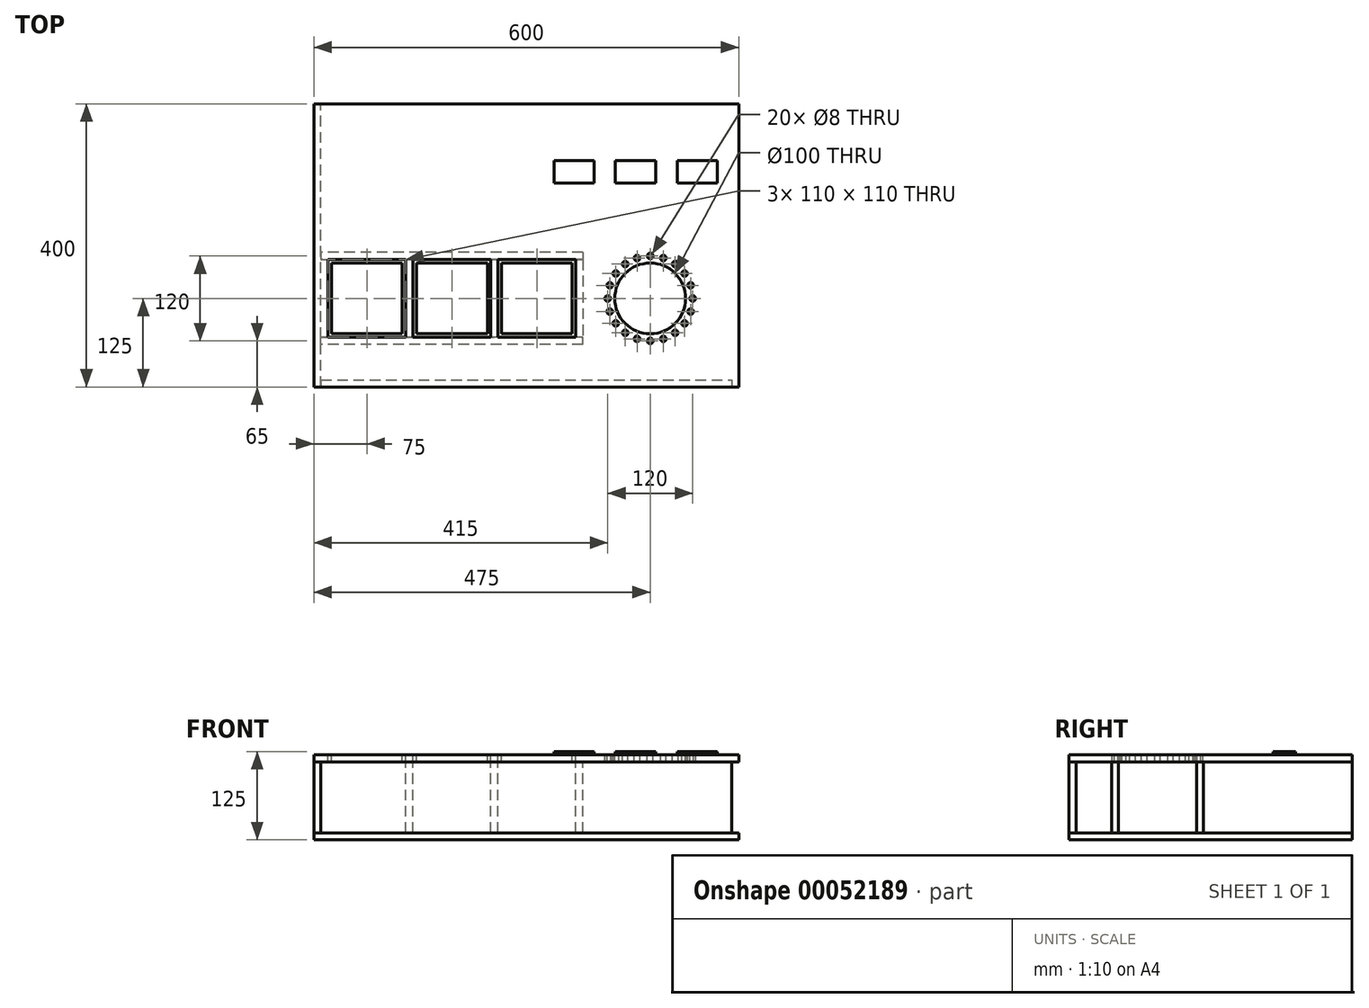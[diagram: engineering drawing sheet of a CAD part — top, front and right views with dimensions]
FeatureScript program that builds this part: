
annotation { "Feature Type Name" : "Feature", "Feature Type Description" : "" }
export const myFeature = defineFeature(function(context is Context, id is Id, definition is map)
    precondition{}
    {
        {
            var Q0;
            Q0=qCreatedBy(makeId("Top.planeOp"),FACE);
            var sketch = newSketch(context, id + "F0", { "sketchPlane" : qUnion([Q0])});
            skLineSegment(sketch, "E0.bottom", {"start": v(0, 0) * mm, "end": v(600, 0) * mm});
            skLineSegment(sketch, "E0.top", {"start": v(0, 400) * mm, "end": v(600, 400) * mm});
            skLineSegment(sketch, "E0.left", {"start": v(0, 0) * mm, "end": v(0, 400) * mm});
            skLineSegment(sketch, "E0.right", {"start": v(600, 0) * mm, "end": v(600, 400) * mm});
            skSolve(sketch);
        }
        {
            var Q0;
            Q0 = qSketchRegion(id + "F0", true);
            extrude(context, id + "F1", {"entities" : qUnion([Q0]), "oppositeDirection" : true, "depth" : 10 * mm});
        }
        {
            var Q0;
            Q0=qCreatedBy(makeId("Right.planeOp"),FACE);
            var sketch = newSketch(context, id + "F2", { "sketchPlane" : qUnion([Q0])});
            skLineSegment(sketch, "E1.bottom", {"start": v(0, 0) * mm, "end": v(400, 0) * mm});
            skLineSegment(sketch, "E1.top", {"start": v(0, 100) * mm, "end": v(400, 100) * mm});
            skLineSegment(sketch, "E1.left", {"start": v(0, 0) * mm, "end": v(0, 100) * mm});
            skLineSegment(sketch, "E1.right", {"start": v(400, 0) * mm, "end": v(400, 100) * mm});
            skSolve(sketch);
        }
        {
            var Q0;
            Q0 = qSketchRegion(id + "F2", true);
            extrude(context, id + "F3", {"entities" : qUnion([Q0]), "depth" : 10 * mm});
        }
        {
            var Q0;
            Q0=qCreatedBy(makeId("Front.planeOp"),FACE);
            var sketch = newSketch(context, id + "F4", { "sketchPlane" : qUnion([Q0])});
            skLineSegment(sketch, "E2.bottom", {"start": v(10, 0) * mm, "end": v(590, 0) * mm});
            skLineSegment(sketch, "E2.top", {"start": v(10, 100) * mm, "end": v(590, 100) * mm});
            skLineSegment(sketch, "E2.left", {"start": v(10, 0) * mm, "end": v(10, 100) * mm});
            skLineSegment(sketch, "E2.right", {"start": v(590, 0) * mm, "end": v(590, 100) * mm});
            skLineSegment(sketch, "E3", {"start": v(590, 100) * mm, "end": v(600, 100) * mm, "construction": true});
            skSolve(sketch);
        }
        {
            var Q0;
            Q0 = qSketchRegion(id + "F4", true);
            extrude(context, id + "F5", {"entities" : qUnion([Q0]), "oppositeDirection" : true, "depth" : 10 * mm});
        }
        {
            var Q0;
            Q0=makeQuery(id+"F3.opExtrude","SWEPT_FACE",FACE,{"disambiguationData":[OSD([sQuery(id+"F2.wireOp",EDGE,"E1.top")])]});
            var sketch = newSketch(context, id + "F6", { "sketchPlane" : qUnion([Q0])});
            skLineSegment(sketch, "E4.0.0", {"start": v(0, 400) * mm, "end": v(0, 0) * mm});
            skLineSegment(sketch, "E4.0.1", {"start": v(0, 0) * mm, "end": v(600, 0) * mm});
            skLineSegment(sketch, "E4.0.2", {"start": v(600, 0) * mm, "end": v(600, 400) * mm});
            skLineSegment(sketch, "E4.0.3", {"start": v(600, 400) * mm, "end": v(0, 400) * mm});
            skSolve(sketch);
        }
        {
            var Q0;
            Q0 = qSketchRegion(id + "F6", true);
            extrude(context, id + "F7", {"entities" : qUnion([Q0]), "depth" : 10 * mm});
        }
        {
            var Q0;
            Q0=makeQuery(id+"F7.opExtrude","CAP_FACE",FACE,{"disambiguationData":[OSD([sQuery(id+"F6.wireOp",EDGE,"E4.0.0"),sQuery(id+"F6.wireOp",EDGE,"E4.0.1"),sQuery(id+"F6.wireOp",EDGE,"E4.0.2"),sQuery(id+"F6.wireOp",EDGE,"E4.0.3")])],"isStart":false});
            var sketch = newSketch(context, id + "F8", { "sketchPlane" : qUnion([Q0])});
            skLineSegment(sketch, "E5.rect.bottom", {"start": v(20, 180) * mm, "end": v(130, 180) * mm});
            skLineSegment(sketch, "E5.rect.top", {"start": v(20, 70) * mm, "end": v(130, 70) * mm});
            skLineSegment(sketch, "E5.rect.left", {"start": v(20, 180) * mm, "end": v(20, 70) * mm});
            skLineSegment(sketch, "E5.rect.right", {"start": v(130, 180) * mm, "end": v(130, 70) * mm});
            skPoint(sketch, "E5.rect.middle", {"position": v(75, 125) * mm});
            skLineSegment(sketch, "E6.rect.bottom", {"start": v(25, 175) * mm, "end": v(125, 175) * mm});
            skLineSegment(sketch, "E6.rect.top", {"start": v(25, 75) * mm, "end": v(125, 75) * mm});
            skLineSegment(sketch, "E6.rect.left", {"start": v(25, 175) * mm, "end": v(25, 75) * mm});
            skLineSegment(sketch, "E6.rect.right", {"start": v(125, 175) * mm, "end": v(125, 75) * mm});
            skLineSegment(sketch, "E7.1.0.0", {"start": v(245, 175) * mm, "end": v(245, 75) * mm});
            skLineSegment(sketch, "E7.1.0.1", {"start": v(145, 75) * mm, "end": v(245, 75) * mm});
            skLineSegment(sketch, "E7.1.0.2", {"start": v(145, 175) * mm, "end": v(145, 75) * mm});
            skLineSegment(sketch, "E7.1.0.3", {"start": v(145, 175) * mm, "end": v(245, 175) * mm});
            skLineSegment(sketch, "E7.1.0.4", {"start": v(140, 180) * mm, "end": v(250, 180) * mm});
            skLineSegment(sketch, "E7.1.0.5", {"start": v(250, 180) * mm, "end": v(250, 70) * mm});
            skLineSegment(sketch, "E7.1.0.6", {"start": v(140, 70) * mm, "end": v(250, 70) * mm});
            skLineSegment(sketch, "E7.1.0.7", {"start": v(140, 180) * mm, "end": v(140, 70) * mm});
            skLineSegment(sketch, "E7.2.0.0", {"start": v(365, 175) * mm, "end": v(365, 75) * mm});
            skLineSegment(sketch, "E7.2.0.1", {"start": v(265, 75) * mm, "end": v(365, 75) * mm});
            skLineSegment(sketch, "E7.2.0.2", {"start": v(265, 175) * mm, "end": v(265, 75) * mm});
            skLineSegment(sketch, "E7.2.0.3", {"start": v(265, 175) * mm, "end": v(365, 175) * mm});
            skLineSegment(sketch, "E7.2.0.4", {"start": v(260, 180) * mm, "end": v(370, 180) * mm});
            skLineSegment(sketch, "E7.2.0.5", {"start": v(370, 180) * mm, "end": v(370, 70) * mm});
            skLineSegment(sketch, "E7.2.0.6", {"start": v(260, 70) * mm, "end": v(370, 70) * mm});
            skLineSegment(sketch, "E7.2.0.7", {"start": v(260, 180) * mm, "end": v(260, 70) * mm});
            skLineSegment(sketch, "E7.direction1", {"start": v(130, 70) * mm, "end": v(250, 70) * mm, "construction": true});
            skSolve(sketch);
        }
        {
            var Q0;
            Q0 = qSketchRegion(id + "F8", true);
            extrude(context, id + "F9", {"entities" : qUnion([Q0]), "operationType" : NewBodyOperationType.REMOVE, "endBound" : BoundingType.UP_TO_NEXT, "oppositeDirection" : true, "depth" : 25 * mm});
        }
        {
            var Q0;
            {var subQ0=sQuery(id+"F6.wireOp",EDGE,"E4.0.1");var subQ1=sQuery(id+"F6.wireOp",EDGE,"E4.0.0");var subQ2=sQuery(id+"F6.wireOp",EDGE,"E4.0.2");var subQ3=sQuery(id+"F6.wireOp",EDGE,"E4.0.3");Q0=makeQuery(id+"F9.boolean.opBoolean","SPLIT",FACE,{"disambiguationData":[TD([makeQuery(id+"F7.opExtrude","SWEPT_FACE",FACE,{"disambiguationData":[OSD([subQ1])]})])],"derivedFrom":makeQuery(id+"F7.opExtrude","CAP_FACE",FACE,{"disambiguationData":[OSD([subQ1,subQ0,subQ2,subQ3])],"isStart":true})});}
            var sketch = newSketch(context, id + "F10", { "sketchPlane" : qUnion([Q0])});
            skLineSegment(sketch, "E8.bottom", {"start": v(130, -70) * mm, "end": v(140, -70) * mm});
            skLineSegment(sketch, "E8.top", {"start": v(130, -180) * mm, "end": v(140, -180) * mm});
            skLineSegment(sketch, "E8.left", {"start": v(130, -70) * mm, "end": v(130, -180) * mm});
            skLineSegment(sketch, "E8.right", {"start": v(140, -70) * mm, "end": v(140, -180) * mm});
            skLineSegment(sketch, "E9.bottom", {"start": v(250, -70) * mm, "end": v(260, -70) * mm});
            skLineSegment(sketch, "E9.top", {"start": v(250, -180) * mm, "end": v(260, -180) * mm});
            skLineSegment(sketch, "E9.left", {"start": v(250, -70) * mm, "end": v(250, -180) * mm});
            skLineSegment(sketch, "E9.right", {"start": v(260, -70) * mm, "end": v(260, -180) * mm});
            skLineSegment(sketch, "E10.bottom", {"start": v(370, -70) * mm, "end": v(380, -70) * mm});
            skLineSegment(sketch, "E10.top", {"start": v(370, -180) * mm, "end": v(380, -180) * mm});
            skLineSegment(sketch, "E10.left", {"start": v(370, -70) * mm, "end": v(370, -180) * mm});
            skLineSegment(sketch, "E10.right", {"start": v(380, -70) * mm, "end": v(380, -180) * mm});
            skSolve(sketch);
        }
        {
            var Q0;
            Q0 = qSketchRegion(id + "F10", true);
            extrude(context, id + "F11", {"entities" : qUnion([Q0]), "endBound" : BoundingType.UP_TO_NEXT, "depth" : 25 * mm});
        }
        {
            var Q0;
            {var subQ0=sQuery(id+"F6.wireOp",EDGE,"E4.0.1");var subQ1=sQuery(id+"F6.wireOp",EDGE,"E4.0.0");var subQ2=sQuery(id+"F6.wireOp",EDGE,"E4.0.2");var subQ3=sQuery(id+"F6.wireOp",EDGE,"E4.0.3");Q0=makeQuery(id+"F9.boolean.opBoolean","SPLIT",FACE,{"disambiguationData":[TD([makeQuery(id+"F7.opExtrude","SWEPT_FACE",FACE,{"disambiguationData":[OSD([subQ1])]})])],"derivedFrom":makeQuery(id+"F7.opExtrude","CAP_FACE",FACE,{"disambiguationData":[OSD([subQ1,subQ0,subQ2,subQ3])],"isStart":true})});}
            var sketch = newSketch(context, id + "F12", { "sketchPlane" : qUnion([Q0])});
            skLineSegment(sketch, "E11.bottom", {"start": v(10, -180) * mm, "end": v(380, -180) * mm});
            skLineSegment(sketch, "E11.top", {"start": v(10, -190) * mm, "end": v(380, -190) * mm});
            skLineSegment(sketch, "E11.left", {"start": v(10, -180) * mm, "end": v(10, -190) * mm});
            skLineSegment(sketch, "E11.right", {"start": v(380, -180) * mm, "end": v(380, -190) * mm});
            skLineSegment(sketch, "E12", {"start": v(75, -125) * mm, "end": v(338.85, -125) * mm, "construction": true});
            skLineSegment(sketch, "E13", {"start": v(20, -180) * mm, "end": v(130, -70) * mm, "construction": true});
            skLineSegment(sketch, "E14", {"start": v(20, -70) * mm, "end": v(130, -180) * mm, "construction": true});
            skLineSegment(sketch, "E15.MirrorCS", {"start": v(10, -70) * mm, "end": v(380, -70) * mm});
            skLineSegment(sketch, "E16.MirrorCS", {"start": v(10, -60) * mm, "end": v(380, -60) * mm});
            skLineSegment(sketch, "E17.MirrorCS", {"start": v(10, -70) * mm, "end": v(10, -60) * mm});
            skLineSegment(sketch, "E18.MirrorCS", {"start": v(380, -70) * mm, "end": v(380, -60) * mm});
            skSolve(sketch);
        }
        {
            var Q0;
            Q0 = qSketchRegion(id + "F12", true);
            extrude(context, id + "F13", {"entities" : qUnion([Q0]), "endBound" : BoundingType.UP_TO_NEXT, "depth" : 25 * mm});
        }
        {
            var Q0;
            {var subQ0=sQuery(id+"F6.wireOp",EDGE,"E4.0.1");var subQ1=sQuery(id+"F6.wireOp",EDGE,"E4.0.0");var subQ2=sQuery(id+"F6.wireOp",EDGE,"E4.0.2");var subQ3=sQuery(id+"F6.wireOp",EDGE,"E4.0.3");Q0=makeQuery(id+"F9.boolean.opBoolean","SPLIT",FACE,{"disambiguationData":[TD([makeQuery(id+"F7.opExtrude","SWEPT_FACE",FACE,{"disambiguationData":[OSD([subQ1])]})])],"derivedFrom":makeQuery(id+"F7.opExtrude","CAP_FACE",FACE,{"disambiguationData":[OSD([subQ1,subQ0,subQ2,subQ3])],"isStart":false})});}
            var sketch = newSketch(context, id + "F14", { "sketchPlane" : qUnion([Q0])});
            skCircle(sketch, "E19", {"center": v(475, 125) * mm, "radius": 50 * mm});
            skLineSegment(sketch, "E20", {"start": v(260, 70) * mm, "end": v(370, 180) * mm, "construction": true});
            skPoint(sketch, "E21", {"position": v(315, 125) * mm});
            skCircle(sketch, "E22", {"center": v(475, 125) * mm, "radius": 60 * mm, "construction": true});
            skLineSegment(sketch, "E23", {"start": v(475, 125) * mm, "end": v(415, 125) * mm, "construction": true});
            skCircle(sketch, "E24", {"center": v(415, 125) * mm, "radius": 4 * mm});
            skCircle(sketch, "E25.1.0", {"center": v(417.94, 106.46) * mm, "radius": 4 * mm});
            skCircle(sketch, "E25.2.0", {"center": v(426.46, 89.73) * mm, "radius": 4 * mm});
            skCircle(sketch, "E25.3.0", {"center": v(439.73, 76.46) * mm, "radius": 4 * mm});
            skCircle(sketch, "E25.4.0", {"center": v(456.46, 67.94) * mm, "radius": 4 * mm});
            skCircle(sketch, "E25.5.0", {"center": v(475, 65) * mm, "radius": 4 * mm});
            skCircle(sketch, "E25.6.0", {"center": v(493.54, 67.94) * mm, "radius": 4 * mm});
            skCircle(sketch, "E25.7.0", {"center": v(510.27, 76.46) * mm, "radius": 4 * mm});
            skCircle(sketch, "E25.8.0", {"center": v(523.54, 89.73) * mm, "radius": 4 * mm});
            skCircle(sketch, "E25.9.0", {"center": v(532.06, 106.46) * mm, "radius": 4 * mm});
            skLineSegment(sketch, "E25.anchor2", {"start": v(475, 125) * mm, "end": v(535, 125) * mm, "construction": true});
            skCircle(sketch, "E26.MirrorC", {"center": v(523.54, 160.27) * mm, "radius": 4 * mm});
            skCircle(sketch, "E27.MirrorC", {"center": v(510.27, 173.54) * mm, "radius": 4 * mm});
            skCircle(sketch, "E28.MirrorC", {"center": v(493.54, 182.06) * mm, "radius": 4 * mm});
            skCircle(sketch, "E29.MirrorC", {"center": v(475, 185) * mm, "radius": 4 * mm});
            skCircle(sketch, "E30.MirrorC", {"center": v(456.46, 182.06) * mm, "radius": 4 * mm});
            skCircle(sketch, "E31.MirrorC", {"center": v(439.73, 173.54) * mm, "radius": 4 * mm});
            skCircle(sketch, "E32.MirrorC", {"center": v(426.46, 160.27) * mm, "radius": 4 * mm});
            skCircle(sketch, "E33.MirrorC", {"center": v(417.94, 143.54) * mm, "radius": 4 * mm});
            skCircle(sketch, "E34.1.10.0", {"center": v(535, 125) * mm, "radius": 4 * mm});
            skCircle(sketch, "E35.MirrorC", {"center": v(532.06, 143.54) * mm, "radius": 4 * mm});
            skSolve(sketch);
        }
        {
            var Q0;
            Q0 = qSketchRegion(id + "F14", true);
            extrude(context, id + "F15", {"entities" : qUnion([Q0]), "operationType" : NewBodyOperationType.REMOVE, "endBound" : BoundingType.UP_TO_NEXT, "oppositeDirection" : true, "depth" : 25 * mm});
        }
        {
            var Q0;
            {var subQ0=sQuery(id+"F6.wireOp",EDGE,"E4.0.1");var subQ1=sQuery(id+"F6.wireOp",EDGE,"E4.0.0");var subQ2=sQuery(id+"F6.wireOp",EDGE,"E4.0.2");var subQ3=sQuery(id+"F6.wireOp",EDGE,"E4.0.3");Q0=makeQuery(id+"F9.boolean.opBoolean","SPLIT",FACE,{"disambiguationData":[TD([makeQuery(id+"F7.opExtrude","SWEPT_FACE",FACE,{"disambiguationData":[OSD([subQ1])]})])],"derivedFrom":makeQuery(id+"F7.opExtrude","CAP_FACE",FACE,{"disambiguationData":[OSD([subQ1,subQ0,subQ2,subQ3])],"isStart":false})});}
            var sketch = newSketch(context, id + "F16", { "sketchPlane" : qUnion([Q0])});
            skLineSegment(sketch, "E36.bottom", {"start": v(570, 320) * mm, "end": v(513, 320) * mm});
            skLineSegment(sketch, "E36.top", {"start": v(570, 288) * mm, "end": v(513, 288) * mm});
            skLineSegment(sketch, "E36.left", {"start": v(570, 320) * mm, "end": v(570, 288) * mm});
            skLineSegment(sketch, "E36.right", {"start": v(513, 320) * mm, "end": v(513, 288) * mm});
            skLineSegment(sketch, "E37", {"start": v(513, 320) * mm, "end": v(570, 288) * mm, "construction": true});
            skPoint(sketch, "E38", {"position": v(541.5, 304) * mm});
            skLineSegment(sketch, "E39.bottom", {"start": v(483, 288) * mm, "end": v(426, 288) * mm});
            skLineSegment(sketch, "E39.top", {"start": v(483, 320) * mm, "end": v(426, 320) * mm});
            skLineSegment(sketch, "E39.left", {"start": v(483, 288) * mm, "end": v(483, 320) * mm});
            skLineSegment(sketch, "E39.right", {"start": v(426, 288) * mm, "end": v(426, 320) * mm});
            skLineSegment(sketch, "E40.bottom", {"start": v(396, 288) * mm, "end": v(339, 288) * mm});
            skLineSegment(sketch, "E40.top", {"start": v(396, 320) * mm, "end": v(339, 320) * mm});
            skLineSegment(sketch, "E40.left", {"start": v(396, 288) * mm, "end": v(396, 320) * mm});
            skLineSegment(sketch, "E40.right", {"start": v(339, 288) * mm, "end": v(339, 320) * mm});
            skSolve(sketch);
        }
        {
            var Q0;
            Q0 = qSketchRegion(id + "F16", true);
            extrude(context, id + "F17", {"entities" : qUnion([Q0]), "depth" : 5 * mm});
        }
    });
